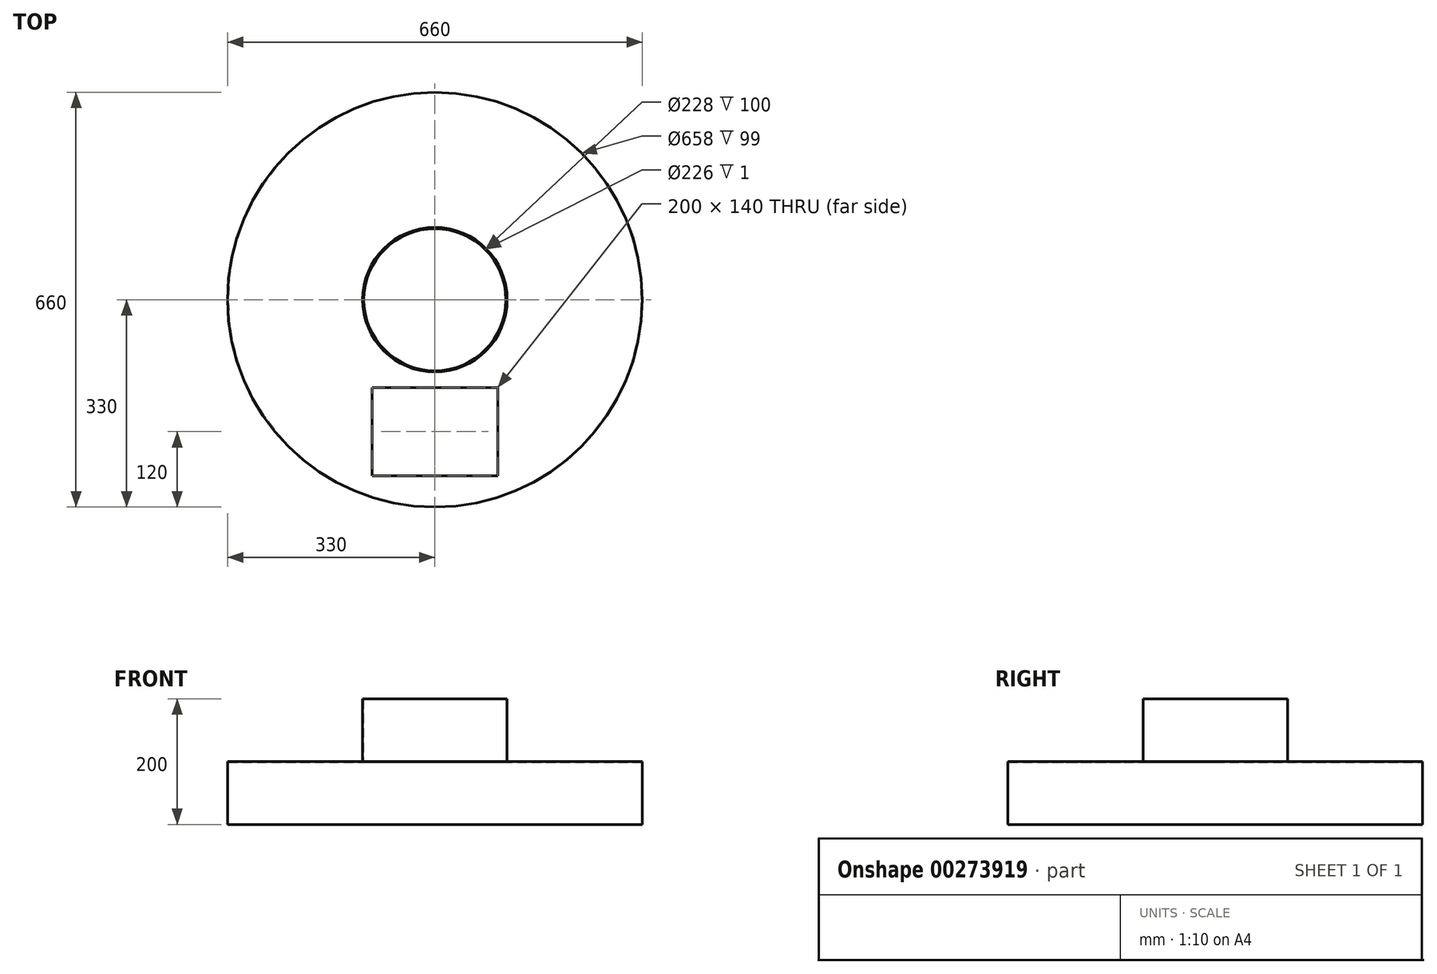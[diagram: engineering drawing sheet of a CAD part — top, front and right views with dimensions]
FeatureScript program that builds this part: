
annotation { "Feature Type Name" : "Feature", "Feature Type Description" : "" }
export const myFeature = defineFeature(function(context is Context, id is Id, definition is map)
    precondition{}
    {
        {
            var Q0;
            Q0=qCreatedBy(makeId("Front.planeOp"),FACE);
            var sketch = newSketch(context, id + "F0", { "sketchPlane" : qUnion([Q0])});
            skLineSegment(sketch, "E0", {"start": v(0, 0) * mm, "end": v(0, 189.83) * mm, "construction": true});
            skLineSegment(sketch, "E1", {"start": v(-115, 100) * mm, "end": v(-115, 0) * mm});
            skLineSegment(sketch, "E2", {"start": v(-115, 0) * mm, "end": v(-330, 0) * mm});
            skLineSegment(sketch, "E3", {"start": v(-330, 0) * mm, "end": v(-330, -100) * mm});
            skLineSegment(sketch, "E4", {"start": v(0, 100) * mm, "end": v(-115, 100) * mm});
            skLineSegment(sketch, "E5", {"start": v(-330, -100) * mm, "end": v(0, -100) * mm});
            skLineSegment(sketch, "E6", {"start": v(0, -100) * mm, "end": v(0, 100) * mm});
            skSolve(sketch);
        }
        {
            var Q0;
            Q0 = qSketchRegion(id + "F0", true);
            var Q1;
            Q1=sQuery(id+"F0.wireOp",EDGE,"E0");
            revolve(context, id + "F1", {"entities" : qUnion([Q0]), "axis" : qUnion([Q1]), "revolveType" : RevolveType.FULL});
        }
        {
            var Q0;
            Q0=makeQuery(id+"F1.opRevolve","SWEPT_FACE",FACE,{"disambiguationData":[OSD([sQuery(id+"F0.wireOp",EDGE,"E5")])]});
            shell(context, id + "F2", {"entities" : qUnion([Q0]), "thickness" : 1 * mm});
        }
        {
            var Q0;
            Q0=makeQuery(id+"F1.opRevolve","SWEPT_FACE",FACE,{"disambiguationData":[OSD([sQuery(id+"F0.wireOp",EDGE,"E4")])]});
            var sketch = newSketch(context, id + "F3", { "sketchPlane" : qUnion([Q0])});
            skCircle(sketch, "E7.0", {"center": v(0, 0) * mm, "radius": 113 * mm});
            skSolve(sketch);
        }
        {
            var Q0;
            Q0 = qSketchRegion(id + "F3", true);
            extrude(context, id + "F4", {"entities" : qUnion([Q0]), "operationType" : NewBodyOperationType.REMOVE, "endBound" : BoundingType.THROUGH_ALL, "oppositeDirection" : true, "depth" : 25 * mm});
        }
        {
            var Q0;
            Q0=makeQuery(id+"F1.opRevolve","SWEPT_FACE",FACE,{"disambiguationData":[OSD([sQuery(id+"F0.wireOp",EDGE,"E2")])]});
            var sketch = newSketch(context, id + "F5", { "sketchPlane" : qUnion([Q0])});
            skLineSegment(sketch, "E8.bottom", {"start": v(100, -140) * mm, "end": v(-100, -140) * mm});
            skLineSegment(sketch, "E8.top", {"start": v(100, -280) * mm, "end": v(-100, -280) * mm});
            skLineSegment(sketch, "E8.left", {"start": v(100, -140) * mm, "end": v(100, -280) * mm});
            skLineSegment(sketch, "E8.right", {"start": v(-100, -140) * mm, "end": v(-100, -280) * mm});
            skSolve(sketch);
        }
        {
            var Q0;
            Q0 = qSketchRegion(id + "F5", true);
            extrude(context, id + "F6", {"entities" : qUnion([Q0]), "operationType" : NewBodyOperationType.REMOVE, "endBound" : BoundingType.THROUGH_ALL, "oppositeDirection" : true, "depth" : 25 * mm});
        }
    });
